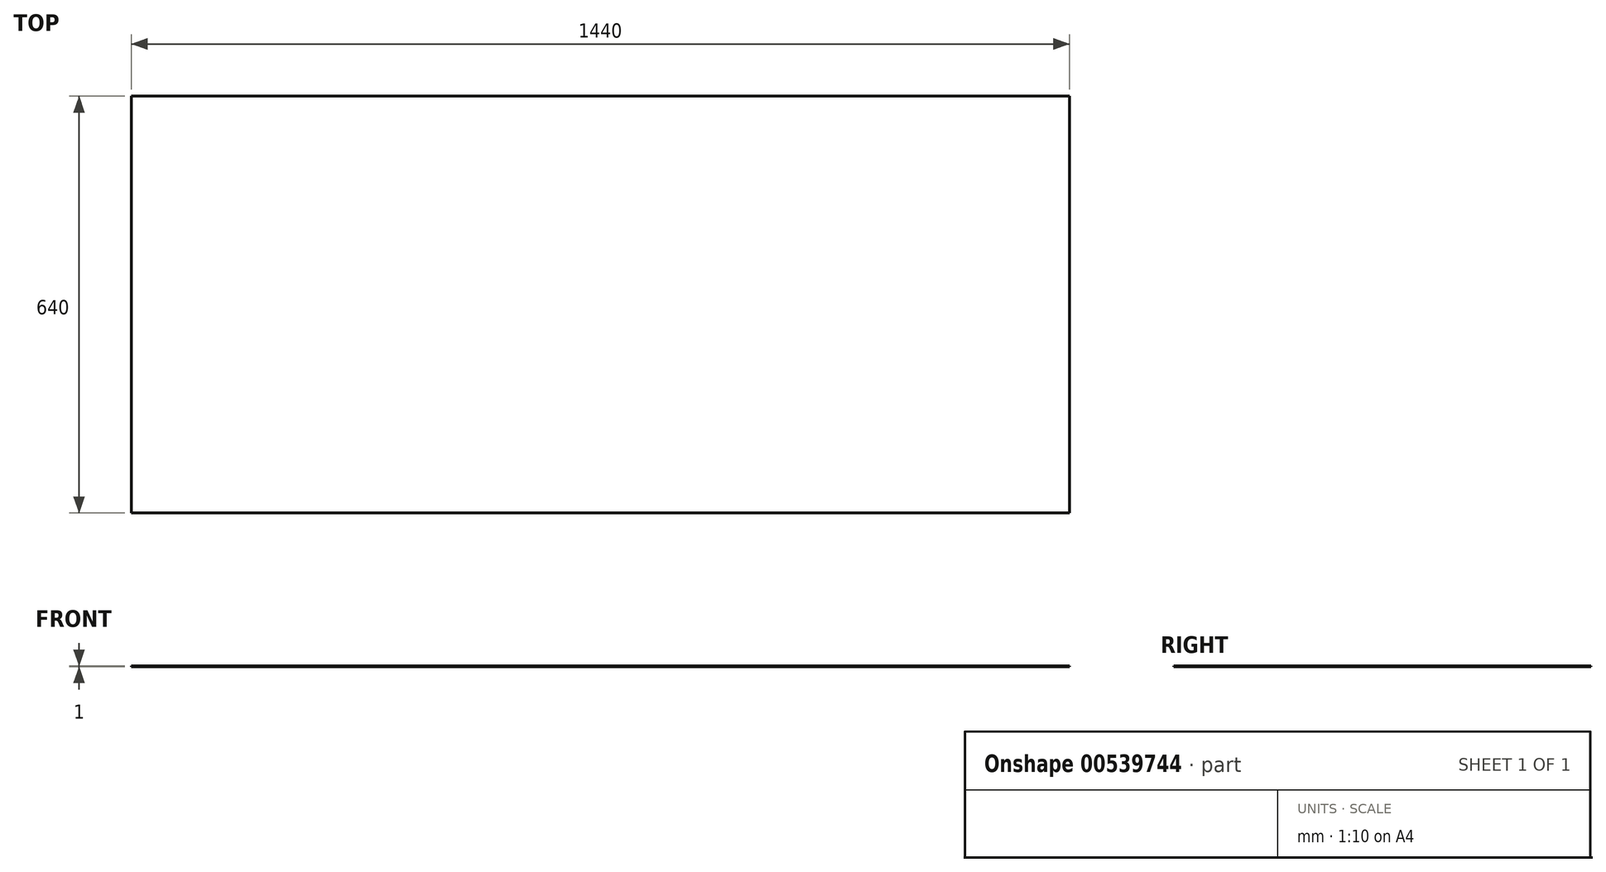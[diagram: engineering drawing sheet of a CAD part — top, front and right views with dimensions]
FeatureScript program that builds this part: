
annotation { "Feature Type Name" : "Feature", "Feature Type Description" : "" }
export const myFeature = defineFeature(function(context is Context, id is Id, definition is map)
    precondition{}
    {
        {
            var Q0;
            Q0=qCreatedBy(makeId("Top.planeOp"),FACE);
            var sketch = newSketch(context, id + "F0", { "sketchPlane" : qUnion([Q0])});
            skLineSegment(sketch, "E0.bottom", {"start": v(0, 0) * mm, "end": v(1450, 0) * mm});
            skLineSegment(sketch, "E0.top", {"start": v(0, 650) * mm, "end": v(1450, 650) * mm});
            skLineSegment(sketch, "E0.left", {"start": v(0, 0) * mm, "end": v(0, 650) * mm});
            skLineSegment(sketch, "E0.right", {"start": v(1450, 0) * mm, "end": v(1450, 650) * mm});
            skLineSegment(sketch, "E1.0", {"start": v(5, 645) * mm, "end": v(1445, 645) * mm});
            skLineSegment(sketch, "E1.1", {"start": v(5, 5) * mm, "end": v(5, 645) * mm});
            skLineSegment(sketch, "E1.2", {"start": v(5, 5) * mm, "end": v(1445, 5) * mm});
            skLineSegment(sketch, "E1.3", {"start": v(1445, 5) * mm, "end": v(1445, 645) * mm});
            skSolve(sketch);
        }
        {
            var Q0;
            Q0=makeQuery(id+"F0.imprint","IMPRINT",FACE,{"disambiguationData":[TD([[makeQuery(id+"F0.imprint","IMPRINT",EDGE,{"derivedFrom":sQuery(id+"F0.wireOp",EDGE,"E1.0")}),-1.0]])]});
            extrude(context, id + "F1", {"entities" : qUnion([Q0]), "depth" : 1 * mm, "offsetDistance" : 25 * mm});
        }
    });
